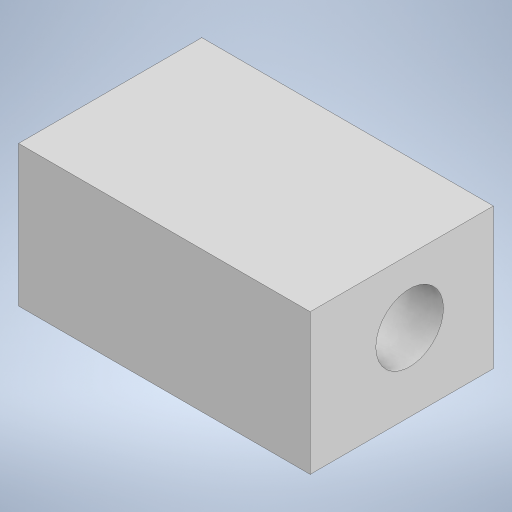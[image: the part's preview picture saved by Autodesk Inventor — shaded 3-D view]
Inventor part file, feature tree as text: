
AUTODESK INVENTOR PART (.ipt)
format: ipt  version: 2024 (Build 280153000, 153)  size: 162,816 bytes
history: native  units: mm
features: sketch x2, extrude x1, hole x1
ambient origin geometry x8: Origin, YZ Plane, XZ Plane, XY Plane, X Axis, Y Axis, Z Axis, Center Point
bodies: Solid1 (feature_tree)
feature tree (4):
  extrude  "Extrusion1"  [1 undecoded]
  hole  "Hole1"  [1 undecoded]
  sketch  "Sketch1"  dims[d0=60.3mm d1=0.0mm]
  sketch  "Sketch2"  dims[d2=14.0mm d3=6.0mm d4=4.0mm d5=2.0mm d6=90.0deg d7=8.0mm d8=20.594885mm]
note: 2 required parameter values undecoded (feature->parameter linkage not recoverable at this tier; creation-order binding heuristic only, values carry confidence <= 0.55)
